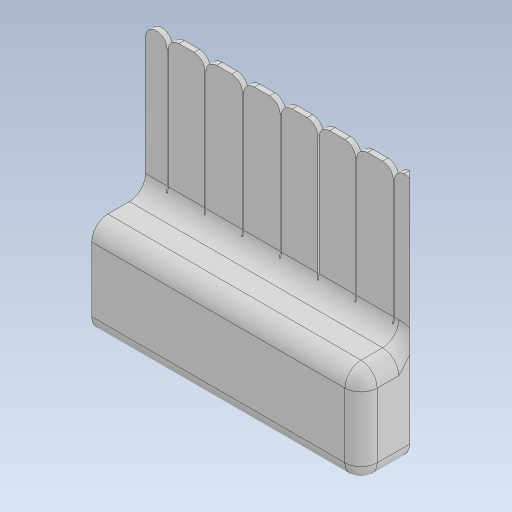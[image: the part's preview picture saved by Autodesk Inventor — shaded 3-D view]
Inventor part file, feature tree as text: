
AUTODESK INVENTOR PART (.ipt)
format: ipt  version: 2023 (Build 270158030, 158C)  size: 249,344 bytes
history: native  units: mm
features: extrude x3, sketch x3, fillet x2, chamfer x1
ambient origin geometry x8: Origin, YZ Plane, XZ Plane, XY Plane, X Axis, Y Axis, Z Axis, Center Point
bodies: Solid1 (feature_tree)
feature tree (9):
  extrude  "Extrusion1"  Depth=45.0mm
  fillet  "Fillet1"  Radius=25.0mm
  extrude  "Extrusion2"  Depth=4.0mm
  fillet  "Fillet2"  Radius=3.8mm
  chamfer  "Chamfer1"  Distance=1.0mm
  extrude  "Extrusion3"  Depth=2.0mm
  sketch  "Sketch1"  dims[d0=50.0mm d1=45.0mm d2=25.0mm]
  sketch  "Sketch2"  dims[d3=0.2mm d4=4.0mm]
  sketch  "Sketch3"  dims[d5=70.0mm d7=7.0mm d8=10.0mm d10=10.0mm d12=3.8mm d13=1.0mm d14=0.0mm d15=2.0mm d16=40.0mm d17=10.0mm d18=18.0mm d19=0.0mm d20=3.0mm d21=6.0mm d22=2.0mm d23=2.0mm d24=45.0deg d25=4.5mm d26=4.5mm d27=4.5mm d28=4.5mm d29=3.0mm d30=0.0mm]
